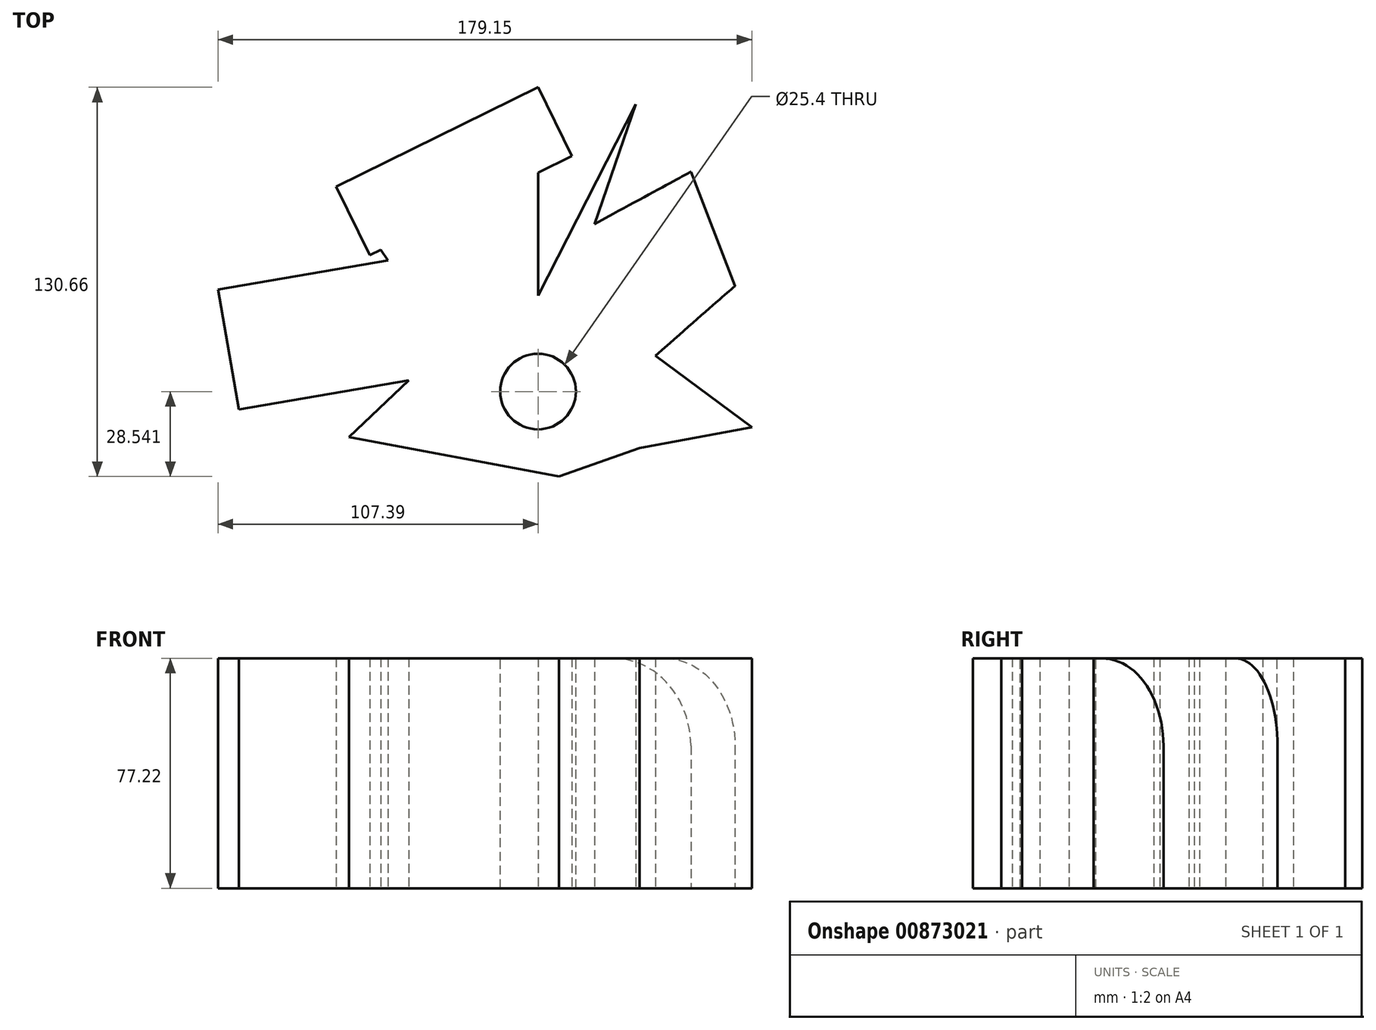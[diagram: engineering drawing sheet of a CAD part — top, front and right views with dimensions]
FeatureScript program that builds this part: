
annotation { "Feature Type Name" : "Feature", "Feature Type Description" : "" }
export const myFeature = defineFeature(function(context is Context, id is Id, definition is map)
    precondition{}
    {
        {
            var Q0;
            Q0=qCreatedBy(makeId("Top.planeOp"),FACE);
            var sketch = newSketch(context, id + "F0", { "sketchPlane" : qUnion([Q0])});
            skLineSegment(sketch, "E0", {"start": v(0, 0) * mm, "end": v(0, 69.95) * mm});
            skLineSegment(sketch, "E1", {"start": v(0, 69.95) * mm, "end": v(-67.8, 36.62) * mm});
            skLineSegment(sketch, "E2", {"start": v(-67.8, 36.62) * mm, "end": v(-50.32, 11.88) * mm});
            skLineSegment(sketch, "E3", {"start": v(-50.32, 11.88) * mm, "end": v(-43.39, -28.37) * mm});
            skLineSegment(sketch, "E4", {"start": v(-43.39, -28.37) * mm, "end": v(-63.51, -47.51) * mm});
            skLineSegment(sketch, "E5", {"start": v(-63.51, -47.51) * mm, "end": v(7.1, -60.7) * mm});
            skLineSegment(sketch, "E6", {"start": v(7.1, -60.7) * mm, "end": v(34.15, -51.14) * mm});
            skLineSegment(sketch, "E7", {"start": v(34.15, -51.14) * mm, "end": v(71.76, -44.21) * mm});
            skLineSegment(sketch, "E8", {"start": v(71.76, -44.21) * mm, "end": v(39.43, -20.13) * mm});
            skLineSegment(sketch, "E9", {"start": v(39.43, -20.13) * mm, "end": v(66.15, 3.3) * mm});
            skLineSegment(sketch, "E10", {"start": v(66.15, 3.3) * mm, "end": v(51.3, 41.57) * mm});
            skLineSegment(sketch, "E11", {"start": v(51.3, 41.57) * mm, "end": v(18.97, 24.09) * mm});
            skLineSegment(sketch, "E12", {"start": v(18.97, 24.09) * mm, "end": v(32.83, 64.34) * mm});
            skLineSegment(sketch, "E13", {"start": v(32.83, 64.34) * mm, "end": v(0, 0) * mm});
            skSolve(sketch);
        }
        {
            var Q0;
            Q0=makeQuery(id+"F0.imprint","IMPRINT",FACE,{"disambiguationData":[TD([[makeQuery(id+"F0.imprint","IMPRINT",EDGE,{"derivedFrom":sQuery(id+"F0.wireOp",EDGE,"E0")}),1.0]])]});
            extrude(context, id + "F1", {"entities" : qUnion([Q0]), "depth" : 77.22 * mm, "offsetDistance" : 25.4 * mm});
        }
        {
            var Q0;
            Q0=makeQuery(id+"F1.opExtrude","CAP_EDGE",EDGE,{"disambiguationData":[OSD([sQuery(id+"F0.wireOp",EDGE,"E10")])],"isStart":false});
            fillet(context, id + "F2", {"entities" : qUnion([Q0]), "radius" : 29.43 * mm, "tangentPropagation" : true, "allowEdgeOverflow" : false});
        }
        {
            var Q0;
            Q0=makeQuery(id+"F1.opExtrude","CAP_FACE",FACE,{"disambiguationData":[OSD([sQuery(id+"F0.wireOp",EDGE,"E0"),sQuery(id+"F0.wireOp",EDGE,"E1"),sQuery(id+"F0.wireOp",EDGE,"E2"),sQuery(id+"F0.wireOp",EDGE,"E3"),sQuery(id+"F0.wireOp",EDGE,"E4"),sQuery(id+"F0.wireOp",EDGE,"E5"),sQuery(id+"F0.wireOp",EDGE,"E6"),sQuery(id+"F0.wireOp",EDGE,"E7"),sQuery(id+"F0.wireOp",EDGE,"E8"),sQuery(id+"F0.wireOp",EDGE,"E9"),sQuery(id+"F0.wireOp",EDGE,"E10"),sQuery(id+"F0.wireOp",EDGE,"E11"),sQuery(id+"F0.wireOp",EDGE,"E12"),sQuery(id+"F0.wireOp",EDGE,"E13")])],"isStart":false});
            var sketch = newSketch(context, id + "F3", { "sketchPlane" : qUnion([Q0])});
            skCircle(sketch, "E14", {"center": v(0, -32.17) * mm, "radius": 14.62 * mm});
            skPoint(sketch, "E14.centerSnap0", {"position": v(55.6, -32.17) * mm});
            skSolve(sketch);
        }
        {
            var Q0;
            Q0=sQuery(id+"F3.wireOp",VERTEX,"E14.center");
            var Q1;
            Q1=makeQuery(id+"F1.opExtrude","SWEPT_BODY",BODY,{"disambiguationData":[OSD([sQuery(id+"F0.wireOp",EDGE,"E0"),sQuery(id+"F0.wireOp",EDGE,"E1"),sQuery(id+"F0.wireOp",EDGE,"E2"),sQuery(id+"F0.wireOp",EDGE,"E3"),sQuery(id+"F0.wireOp",EDGE,"E4"),sQuery(id+"F0.wireOp",EDGE,"E5"),sQuery(id+"F0.wireOp",EDGE,"E6"),sQuery(id+"F0.wireOp",EDGE,"E7"),sQuery(id+"F0.wireOp",EDGE,"E8"),sQuery(id+"F0.wireOp",EDGE,"E9"),sQuery(id+"F0.wireOp",EDGE,"E10"),sQuery(id+"F0.wireOp",EDGE,"E11"),sQuery(id+"F0.wireOp",EDGE,"E12"),sQuery(id+"F0.wireOp",EDGE,"E13")])]});
            hole(context, id + "F4", {"style" : HoleStyle.SIMPLE, "endStyle" : HoleEndStyle.THROUGH, "holeDiameter" : 25.4 * mm, "majorDiameter" : 6.35 * mm, "isTappedThrough" : true, "tappedDepth" : 12.7 * mm, "tapClearance" : 3, "locations" : qUnion([Q0]), "scope" : qUnion([Q1])});
        }
        {
            var Q0;
            Q0=makeQuery(id+"F1.opExtrude","SWEPT_FACE",FACE,{"disambiguationData":[OSD([sQuery(id+"F0.wireOp",EDGE,"E1")])]});
            extrude(context, id + "F5", {"entities" : qUnion([Q0]), "operationType" : NewBodyOperationType.ADD, "oppositeDirection" : true, "depth" : 25.65 * mm, "offsetDistance" : 25.4 * mm});
        }
        {
            var Q0;
            Q0=makeQuery(id+"F1.opExtrude","SWEPT_FACE",FACE,{"disambiguationData":[OSD([sQuery(id+"F0.wireOp",EDGE,"E3")])]});
            extrude(context, id + "F6", {"entities" : qUnion([Q0]), "operationType" : NewBodyOperationType.ADD, "depth" : 57.9 * mm, "offsetDistance" : 25.4 * mm});
        }
    });
